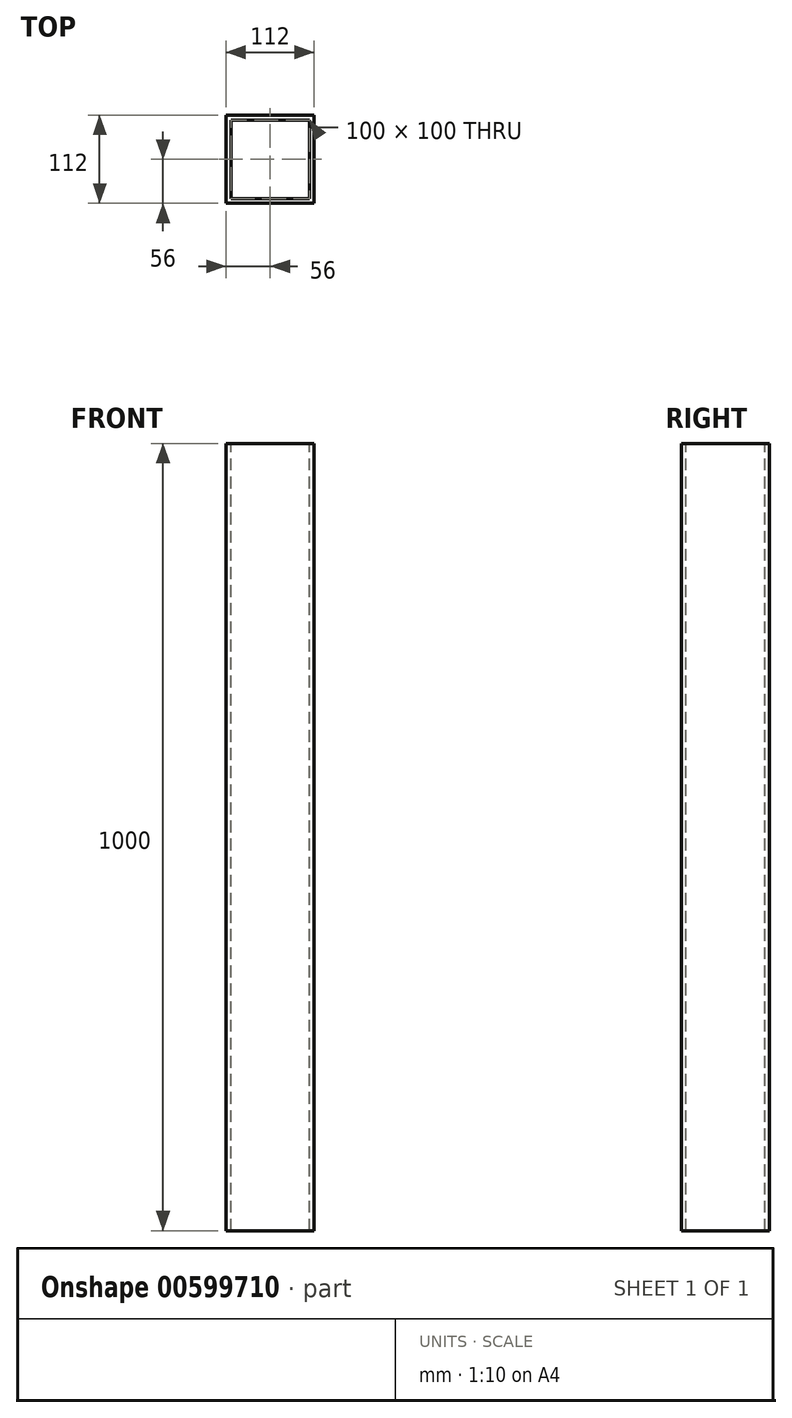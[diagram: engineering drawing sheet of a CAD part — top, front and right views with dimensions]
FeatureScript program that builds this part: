
annotation { "Feature Type Name" : "Feature", "Feature Type Description" : "" }
export const myFeature = defineFeature(function(context is Context, id is Id, definition is map)
    precondition{}
    {
        {
            var Q0;
            Q0=qCreatedBy(makeId("Top.planeOp"),FACE);
            var sketch = newSketch(context, id + "F0", { "sketchPlane" : qUnion([Q0])});
            skLineSegment(sketch, "E0.bottom", {"start": v(-56, 56) * mm, "end": v(56, 56) * mm});
            skLineSegment(sketch, "E0.top", {"start": v(-56, -56) * mm, "end": v(56, -56) * mm});
            skLineSegment(sketch, "E0.left", {"start": v(-56, 56) * mm, "end": v(-56, -56) * mm});
            skLineSegment(sketch, "E0.right", {"start": v(56, 56) * mm, "end": v(56, -56) * mm});
            skLineSegment(sketch, "E1.bottom", {"start": v(-50, 50) * mm, "end": v(50, 50) * mm});
            skLineSegment(sketch, "E1.top", {"start": v(-50, -50) * mm, "end": v(50, -50) * mm});
            skLineSegment(sketch, "E1.left", {"start": v(-50, 50) * mm, "end": v(-50, -50) * mm});
            skLineSegment(sketch, "E1.right", {"start": v(50, 50) * mm, "end": v(50, -50) * mm});
            skSolve(sketch);
        }
        {
            var Q0;
            Q0=makeQuery(id+"F0.imprint","IMPRINT",FACE,{"disambiguationData":[TD([[makeQuery(id+"F0.imprint","IMPRINT",EDGE,{"derivedFrom":sQuery(id+"F0.wireOp",EDGE,"E0.bottom")}),-1.0]])]});
            extrude(context, id + "F1", {"entities" : qUnion([Q0]), "oppositeDirection" : true, "depth" : 1000 * mm, "offsetDistance" : 25 * mm});
        }
    });
